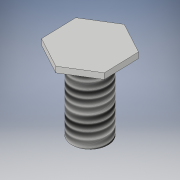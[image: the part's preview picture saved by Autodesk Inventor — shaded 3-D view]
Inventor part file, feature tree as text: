
AUTODESK INVENTOR PART (.ipt)
format: ipt  version: 2017 (Build 210142000, 142)  size: 113,152 bytes
history: native  units: in
note: dims shown in document units (in); Inventor stores cm internally (conversion verified against a paired STEP export)
features: thread x3, extrude x2, sketch x2
ambient origin geometry x8: Origin, YZ Plane, XZ Plane, XY Plane, X Axis, Y Axis, Z Axis, Center Point
bodies: Solid1 (feature_tree)
feature tree (7):
  extrude  "Extrusion1"  Depth=0.25in
  thread  "Thread1"  [1 undecoded]
  extrude  "Extrusion3"  Depth=0.02in TaperAngle=0.0deg
  thread  "Thread3"  [1 undecoded]
  thread  "Thread4"  [1 undecoded]
  sketch  "Sketch1"  dims[d0=0.5in d1=0.125in d2=0.25in d3=0.0in]
  sketch  "Sketch3"  dims[d7=1.0in d8=0.0in d11=0.02in d12=0.0in d13=1.0in d14=0.0in d15=1.0in d16=0.0in]
note: 3 required parameter values undecoded (feature->parameter linkage not recoverable at this tier; creation-order binding heuristic only, values carry confidence <= 0.55)
